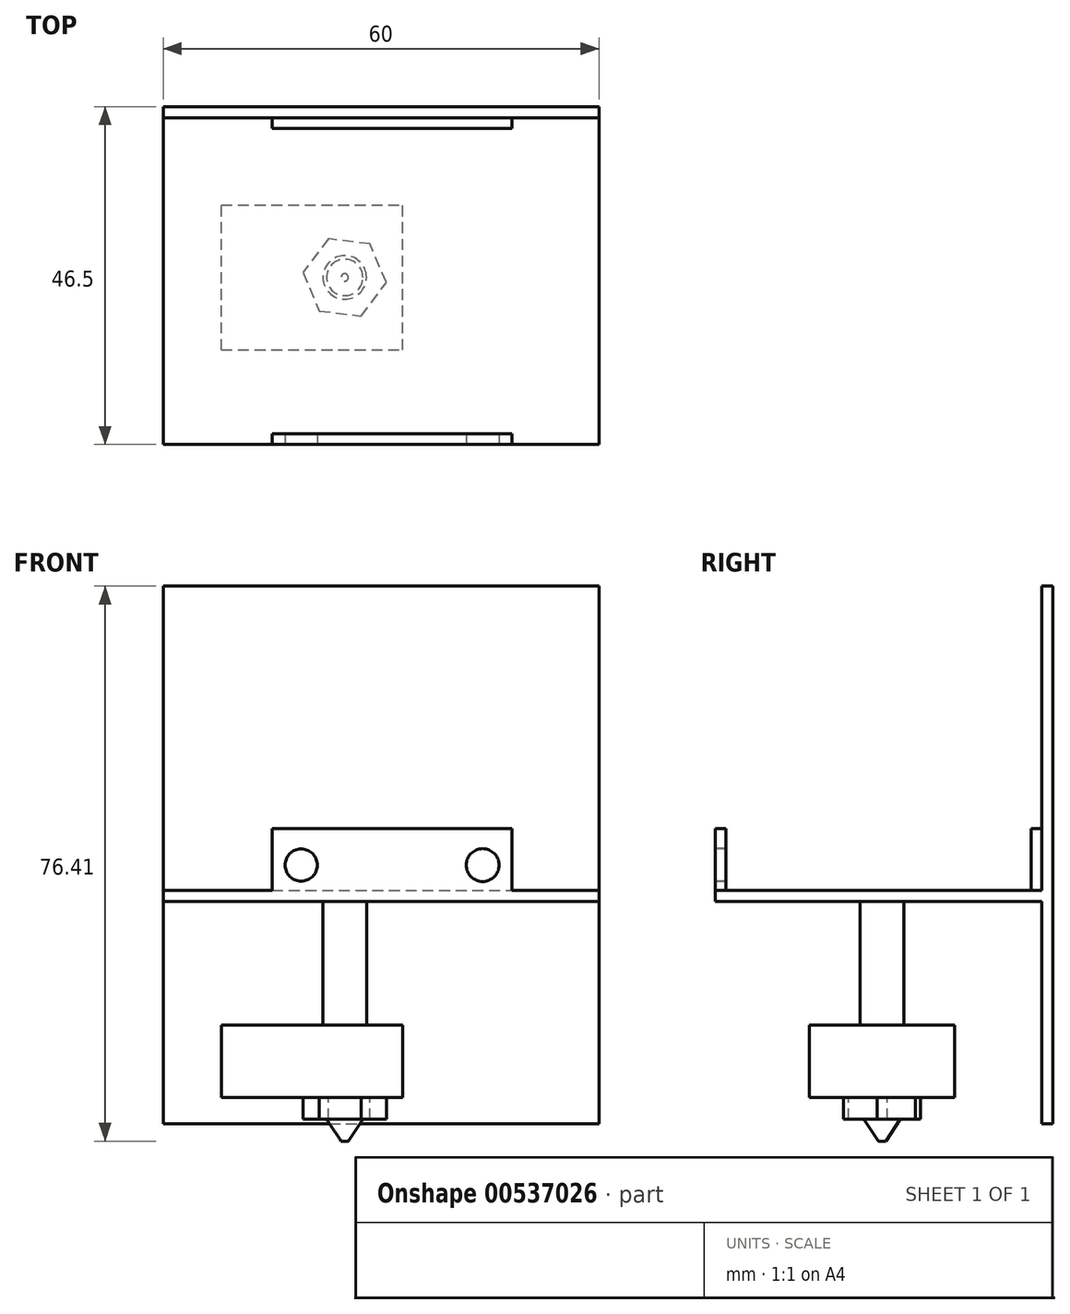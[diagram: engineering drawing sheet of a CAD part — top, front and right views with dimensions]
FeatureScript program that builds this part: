
annotation { "Feature Type Name" : "Feature", "Feature Type Description" : "" }
export const myFeature = defineFeature(function(context is Context, id is Id, definition is map)
    precondition{}
    {
        {
            var Q0;
            Q0=qCreatedBy(makeId("Front.planeOp"),FACE);
            var sketch = newSketch(context, id + "F0", { "sketchPlane" : qUnion([Q0])});
            skLineSegment(sketch, "E0.bottom", {"start": v(-30.6, 54) * mm, "end": v(29.4, 54) * mm});
            skLineSegment(sketch, "E0.top", {"start": v(-30.6, -20) * mm, "end": v(29.4, -20) * mm});
            skLineSegment(sketch, "E0.left", {"start": v(-30.6, 54) * mm, "end": v(-30.6, -20) * mm});
            skLineSegment(sketch, "E0.right", {"start": v(29.4, 54) * mm, "end": v(29.4, -20) * mm});
            skSolve(sketch);
        }
        {
            var Q0;
            Q0=makeQuery(id+"F0.imprint","IMPRINT",FACE,{"disambiguationData":[TD([[makeQuery(id+"F0.imprint","IMPRINT",EDGE,{"derivedFrom":sQuery(id+"F0.wireOp",EDGE,"E0.bottom")}),-1.0]])]});
            extrude(context, id + "F1", {"entities" : qUnion([Q0]), "depth" : 1.5 * mm, "offsetDistance" : 25 * mm});
        }
        {
            var Q0;
            Q0=makeQuery(id+"F1.opExtrude","CAP_FACE",FACE,{"disambiguationData":[OSD([sQuery(id+"F0.wireOp",EDGE,"E0.bottom"),sQuery(id+"F0.wireOp",EDGE,"E0.top"),sQuery(id+"F0.wireOp",EDGE,"E0.left"),sQuery(id+"F0.wireOp",EDGE,"E0.right")])],"isStart":false});
            var sketch = newSketch(context, id + "F2", { "sketchPlane" : qUnion([Q0])});
            skLineSegment(sketch, "E1.bottom", {"start": v(-15.6, 20.6) * mm, "end": v(17.4, 20.6) * mm});
            skLineSegment(sketch, "E1.top", {"start": v(-15.6, 10.6) * mm, "end": v(17.4, 10.6) * mm});
            skLineSegment(sketch, "E1.left", {"start": v(-15.6, 20.6) * mm, "end": v(-15.6, 10.6) * mm});
            skLineSegment(sketch, "E1.right", {"start": v(17.4, 20.6) * mm, "end": v(17.4, 10.6) * mm});
            skSolve(sketch);
        }
        {
            var Q0;
            Q0=makeQuery(id+"F2.imprint","IMPRINT",FACE,{"disambiguationData":[TD([[makeQuery(id+"F2.imprint","IMPRINT",EDGE,{"derivedFrom":sQuery(id+"F2.wireOp",EDGE,"E1.bottom")}),-1.0]])]});
            extrude(context, id + "F3", {"entities" : qUnion([Q0]), "depth" : 1.5 * mm, "offsetDistance" : 25 * mm});
        }
        {
            var Q0;
            Q0=makeQuery(id+"F3.opExtrude","SWEPT_FACE",FACE,{"disambiguationData":[OSD([sQuery(id+"F2.wireOp",EDGE,"E1.top")])]});
            var sketch = newSketch(context, id + "F4", { "sketchPlane" : qUnion([Q0])});
            skLineSegment(sketch, "E2.bottom", {"start": v(-30.6, 1.5) * mm, "end": v(29.4, 1.5) * mm});
            skLineSegment(sketch, "E2.top", {"start": v(-30.6, 46.5) * mm, "end": v(29.4, 46.5) * mm});
            skLineSegment(sketch, "E2.left", {"start": v(-30.6, 1.5) * mm, "end": v(-30.6, 46.5) * mm});
            skLineSegment(sketch, "E2.right", {"start": v(29.4, 1.5) * mm, "end": v(29.4, 46.5) * mm});
            skSolve(sketch);
        }
        {
            var Q0;
            Q0=makeQuery(id+"F4.imprint","IMPRINT",FACE,{"disambiguationData":[TD([[makeQuery(id+"F4.imprint","IMPRINT",EDGE,{"derivedFrom":sQuery(id+"F4.wireOp",EDGE,"E2.top")}),-1.0]])]});
            extrude(context, id + "F5", {"entities" : qUnion([Q0]), "operationType" : NewBodyOperationType.ADD, "oppositeDirection" : true, "depth" : 1.5 * mm, "offsetDistance" : 25 * mm});
        }
        {
            var Q0;
            Q0=makeQuery(id+"F5.opExtrude","SWEPT_FACE",FACE,{"disambiguationData":[OSD([sQuery(id+"F4.wireOp",EDGE,"E2.top")])]});
            var sketch = newSketch(context, id + "F6", { "sketchPlane" : qUnion([Q0])});
            skLineSegment(sketch, "E3.0.0", {"start": v(-15.6, 20.6) * mm, "end": v(-15.6, 12.1) * mm});
            skLineSegment(sketch, "E3.0.2", {"start": v(17.4, 12.1) * mm, "end": v(17.4, 20.6) * mm});
            skLineSegment(sketch, "E3.0.3", {"start": v(17.4, 20.6) * mm, "end": v(-15.6, 20.6) * mm});
            skLineSegment(sketch, "E4.top", {"start": v(-15.6, 10.6) * mm, "end": v(17.4, 10.6) * mm});
            skLineSegment(sketch, "E4.left", {"start": v(-15.6, 12.1) * mm, "end": v(-15.6, 10.6) * mm});
            skLineSegment(sketch, "E4.right", {"start": v(17.4, 12.1) * mm, "end": v(17.4, 10.6) * mm});
            skSolve(sketch);
        }
        {
            var Q0;
            {var subQ0=sQuery(id+"F6.wireOp",EDGE,"E3.0.0");Q0=makeQuery(id+"F6.imprint","IMPRINT",FACE,{"disambiguationData":[TD([[makeQuery(id+"F6.imprint","IMPRINT",EDGE,{"derivedFrom":subQ0}),1.0]])]});}
            var Q1;
            Q1=makeQuery(id+"F6.imprint","IMPRINT",FACE,{"disambiguationData":[TD([[makeQuery(id+"F6.imprint","IMPRINT",EDGE,{"derivedFrom":sQuery(id+"F6.wireOp",EDGE,"E4.top")}),1.0]])]});
            extrude(context, id + "F7", {"entities" : qUnion([Q0, Q1]), "operationType" : NewBodyOperationType.ADD, "oppositeDirection" : true, "depth" : 1.5 * mm, "offsetDistance" : 25 * mm});
        }
        {
            var Q0;
            Q0=makeQuery(id+"F7.boolean.opBoolean","MERGE",FACE,{"derivedFrom":[makeQuery(id+"F5.opExtrude","SWEPT_FACE",FACE,{"disambiguationData":[OSD([sQuery(id+"F4.wireOp",EDGE,"E2.top")])]}),makeQuery(id+"F7.opExtrude","CAP_FACE",FACE,{"disambiguationData":[OSD([sQuery(id+"F6.wireOp",EDGE,"E3.0.0"),sQuery(id+"F6.wireOp",EDGE,"E3.0.2"),sQuery(id+"F6.wireOp",EDGE,"E3.0.3"),sQuery(id+"F6.wireOp",EDGE,"E4.top"),sQuery(id+"F6.wireOp",EDGE,"E4.left"),sQuery(id+"F6.wireOp",EDGE,"E4.right")])],"isStart":true})]});
            var sketch = newSketch(context, id + "F8", { "sketchPlane" : qUnion([Q0])});
            skLineSegment(sketch, "E5", {"start": v(-43.89, 15.6) * mm, "end": v(56.64, 15.6) * mm, "construction": true});
            skCircle(sketch, "E6", {"center": v(-11.6, 15.6) * mm, "radius": 2.22 * mm});
            skCircle(sketch, "E7", {"center": v(13.4, 15.6) * mm, "radius": 2.26 * mm});
            skSolve(sketch);
        }
        {
            var Q0;
            Q0 = qSketchRegion(id + "F8", true);
            extrude(context, id + "F9", {"entities" : qUnion([Q0]), "operationType" : NewBodyOperationType.REMOVE, "endBound" : BoundingType.SYMMETRIC, "oppositeDirection" : true, "depth" : 5 * mm, "offsetDistance" : 25 * mm});
        }
        {
            var Q0;
            {var subQ0=sQuery(id+"F2.wireOp",EDGE,"E1.top");Q0=makeQuery(id+"F5.boolean.opBoolean","MERGE",FACE,{"derivedFrom":[makeQuery(id+"F3.opExtrude","SWEPT_FACE",FACE,{"disambiguationData":[OSD([subQ0])]}),makeQuery(id+"F5.opExtrude","CAP_FACE",FACE,{"disambiguationData":[OSD([subQ0,sQuery(id+"F2.wireOp",EDGE,"E1.left"),sQuery(id+"F2.wireOp",EDGE,"E1.right"),sQuery(id+"F4.wireOp",EDGE,"E2.bottom"),sQuery(id+"F4.wireOp",EDGE,"E2.top"),sQuery(id+"F4.wireOp",EDGE,"E2.left"),sQuery(id+"F4.wireOp",EDGE,"E2.right")])],"isStart":true})]});}
            var sketch = newSketch(context, id + "F10", { "sketchPlane" : qUnion([Q0])});
            skCircle(sketch, "E8", {"center": v(-5.6, 23.5) * mm, "radius": 3 * mm});
            skSolve(sketch);
        }
        {
            var Q0;
            Q0 = qSketchRegion(id + "F10", true);
            extrude(context, id + "F11", {"entities" : qUnion([Q0]), "depth" : 17 * mm, "offsetDistance" : 25 * mm});
        }
        {
            var Q0;
            Q0=makeQuery(id+"F11.opExtrude","CAP_FACE",FACE,{"disambiguationData":[OSD([sQuery(id+"F10.wireOp",EDGE,"E8")])],"isStart":false});
            var sketch = newSketch(context, id + "F12", { "sketchPlane" : qUnion([Q0])});
            skCircle(sketch, "E9.0.0", {"center": v(-5.6, 23.5) * mm, "radius": 3 * mm});
            skLineSegment(sketch, "E10.bottom", {"start": v(-22.6, 33.5) * mm, "end": v(2.4, 33.5) * mm});
            skLineSegment(sketch, "E10.top", {"start": v(-22.6, 13.5) * mm, "end": v(2.4, 13.5) * mm});
            skLineSegment(sketch, "E10.left", {"start": v(-22.6, 33.5) * mm, "end": v(-22.6, 13.5) * mm});
            skLineSegment(sketch, "E10.right", {"start": v(2.4, 33.5) * mm, "end": v(2.4, 13.5) * mm});
            skSolve(sketch);
        }
        {
            var Q0;
            Q0 = qSketchRegion(id + "F12", true);
            var Q1;
            Q1=makeQuery(id+"F12.imprint","IMPRINT",FACE,{"disambiguationData":[TD([[makeQuery(id+"F12.imprint","IMPRINT",EDGE,{"derivedFrom":sQuery(id+"F12.wireOp",EDGE,"E9.0.0")}),1.0]])]});
            extrude(context, id + "F13", {"entities" : qUnion([Q0, Q1]), "operationType" : NewBodyOperationType.ADD, "depth" : 10 * mm, "offsetDistance" : 25 * mm});
        }
        {
            var Q0;
            Q0=makeQuery(id+"F13.opExtrude","CAP_FACE",FACE,{"disambiguationData":[OSD([sQuery(id+"F12.wireOp",EDGE,"E9.0.0"),sQuery(id+"F12.wireOp",EDGE,"E10.bottom"),sQuery(id+"F12.wireOp",EDGE,"E10.top"),sQuery(id+"F12.wireOp",EDGE,"E10.left"),sQuery(id+"F12.wireOp",EDGE,"E10.right")])],"isStart":false});
            var sketch = newSketch(context, id + "F14", { "sketchPlane" : qUnion([Q0])});
            skCircle(sketch, "E11.cCircle", {"center": v(-5.6, 23.5) * mm, "radius": 5 * mm, "construction": true});
            skLineSegment(sketch, "E11.0", {"start": v(-3.36, 28.82) * mm, "end": v(0.13, 24.21) * mm});
            skLineSegment(sketch, "E11.1", {"start": v(0.13, 24.21) * mm, "end": v(-2.12, 18.9) * mm});
            skLineSegment(sketch, "E11.2", {"start": v(-2.12, 18.9) * mm, "end": v(-7.85, 18.18) * mm});
            skLineSegment(sketch, "E11.3", {"start": v(-7.85, 18.18) * mm, "end": v(-11.33, 22.79) * mm});
            skLineSegment(sketch, "E11.4", {"start": v(-11.33, 22.79) * mm, "end": v(-9.09, 28.1) * mm});
            skLineSegment(sketch, "E11.5", {"start": v(-9.09, 28.1) * mm, "end": v(-3.36, 28.82) * mm});
            skPoint(sketch, "E11.0.midPoint", {"position": v(-1.62, 26.52) * mm});
            skSolve(sketch);
        }
        {
            var Q0;
            Q0=makeQuery(id+"F14.imprint","IMPRINT",FACE,{"disambiguationData":[TD([[makeQuery(id+"F14.imprint","IMPRINT",EDGE,{"derivedFrom":sQuery(id+"F14.wireOp",EDGE,"E11.0")}),-1.0]])]});
            var Q1;
            Q1=makeQuery(id+"F14.imprint","IMPRINT",FACE,{"disambiguationData":[TD([[makeQuery(id+"F14.imprint","IMPRINT",EDGE,{"derivedFrom":makeQuery(id+"F13.opExtrude","CAP_EDGE",EDGE,{"disambiguationData":[OSD([sQuery(id+"F12.wireOp",EDGE,"E9.0.0")])],"isStart":false})}),1.0]])]});
            extrude(context, id + "F15", {"entities" : qUnion([Q0, Q1]), "depth" : 3 * mm, "offsetDistance" : 25 * mm});
        }
        {
            var Q0;
            Q0=makeQuery(id+"F15.opExtrude","CAP_FACE",FACE,{"disambiguationData":[OSD([sQuery(id+"F14.wireOp",EDGE,"E11.0"),sQuery(id+"F14.wireOp",EDGE,"E11.1"),sQuery(id+"F14.wireOp",EDGE,"E11.2"),sQuery(id+"F14.wireOp",EDGE,"E11.3"),sQuery(id+"F14.wireOp",EDGE,"E11.4"),sQuery(id+"F14.wireOp",EDGE,"E11.5")])],"isStart":false});
            var sketch = newSketch(context, id + "F16", { "sketchPlane" : qUnion([Q0])});
            skCircle(sketch, "E12.0", {"center": v(-5.6, 23.5) * mm, "radius": 3 * mm});
            skCircle(sketch, "E13", {"center": v(-5.6, 23.5) * mm, "radius": 2.5 * mm});
            skSolve(sketch);
        }
        {
            var Q0;
            Q0=makeQuery(id+"F16.imprint","IMPRINT",FACE,{"disambiguationData":[TD([[makeQuery(id+"F16.imprint","IMPRINT",EDGE,{"derivedFrom":sQuery(id+"F16.wireOp",EDGE,"E13")}),1.0]])]});
            extrude(context, id + "F17", {"entities" : qUnion([Q0]), "operationType" : NewBodyOperationType.ADD, "depth" : 3 * mm, "offsetDistance" : 25 * mm});
        }
        {
            var Q0;
            Q0=makeQuery(id+"F17.opExtrude","CAP_EDGE",EDGE,{"disambiguationData":[OSD([sQuery(id+"F16.wireOp",EDGE,"E13")])],"isStart":false});
            chamfer(context, id + "F18", {"entities" : qUnion([Q0]), "chamferType" : ChamferType.TWO_OFFSETS, "width1" : 2 * mm, "oppositeDirection" : false, "width2" : 3 * mm, "tangentPropagation" : true});
        }
    });
